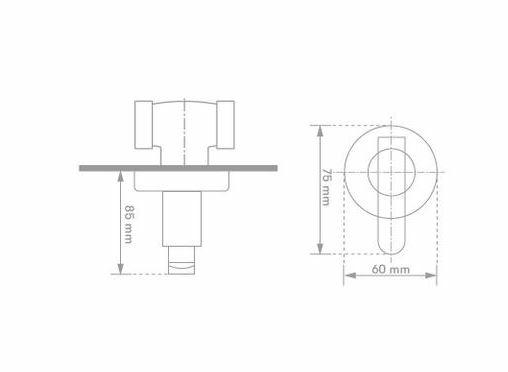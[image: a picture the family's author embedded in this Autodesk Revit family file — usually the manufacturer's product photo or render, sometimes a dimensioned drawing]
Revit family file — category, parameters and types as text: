
# Revit family: 01-0935-11SR-MEZCLADOR HELVETIA
name_source: partatom
category: Aparatos sanitarios
revit_build: Autodesk Revit 2018 (Build: 20170223_1515(x64)
units: mm (PartAtom-declared; Revit-internal decimal feet)

## family parameters
Anfitrión = Cara
Compartido = No
Corte con vacíos al cargar = No
Cota de conector redondo = Diámetro de uso
Número OmniClass = 23.31.11.00
Punto de cálculo de habitación = No
Tipo de pieza = Normal

## types (1)
- 01-0935-11SR
    Alto = 60 mm  [stored 0.19685 ft]
    Ancho = 60 mm  [stored 0.19685 ft]
    Conexión AC = Sí
    Conexión AF = Sí
    Conexión de residuos = No
    Conexión de ventilación = No
    Descripción = Mezclador ducha
    Distancia entre griferias = 203 mm
    Elevación por defecto = 0 mm  [stored 0 ft]
    Fabricante = Gricol
    Imagen de tipo = <Ninguno>
    Link Ficha Tecnica = https://infotecnica.gricol.com
    Metal Acero Inoxidable Cromado = Metal Acero Inoxidable Cromado
    Metal Laton Cromado = Metal Laton Cromado
    Mezclador = Mezclador
    Modelo = 01-0935-11SR
    Plastico ABS Cromado = Plastico ABS Cromado
    Product Name = MEZCLADOR HELVETIA SIN REGADERA
    Profundidad = 85 mm  [stored 0.278871 ft]
    URL = https://www.gricol.com

note: [stored X ft] marks values corroborated as IEEE doubles in the binary element streams (Revit-internal decimal feet)

## geometry (parser evidence)
native form markers: Blend x2, Sweep x8
no freeform markers — native parametric forms only
